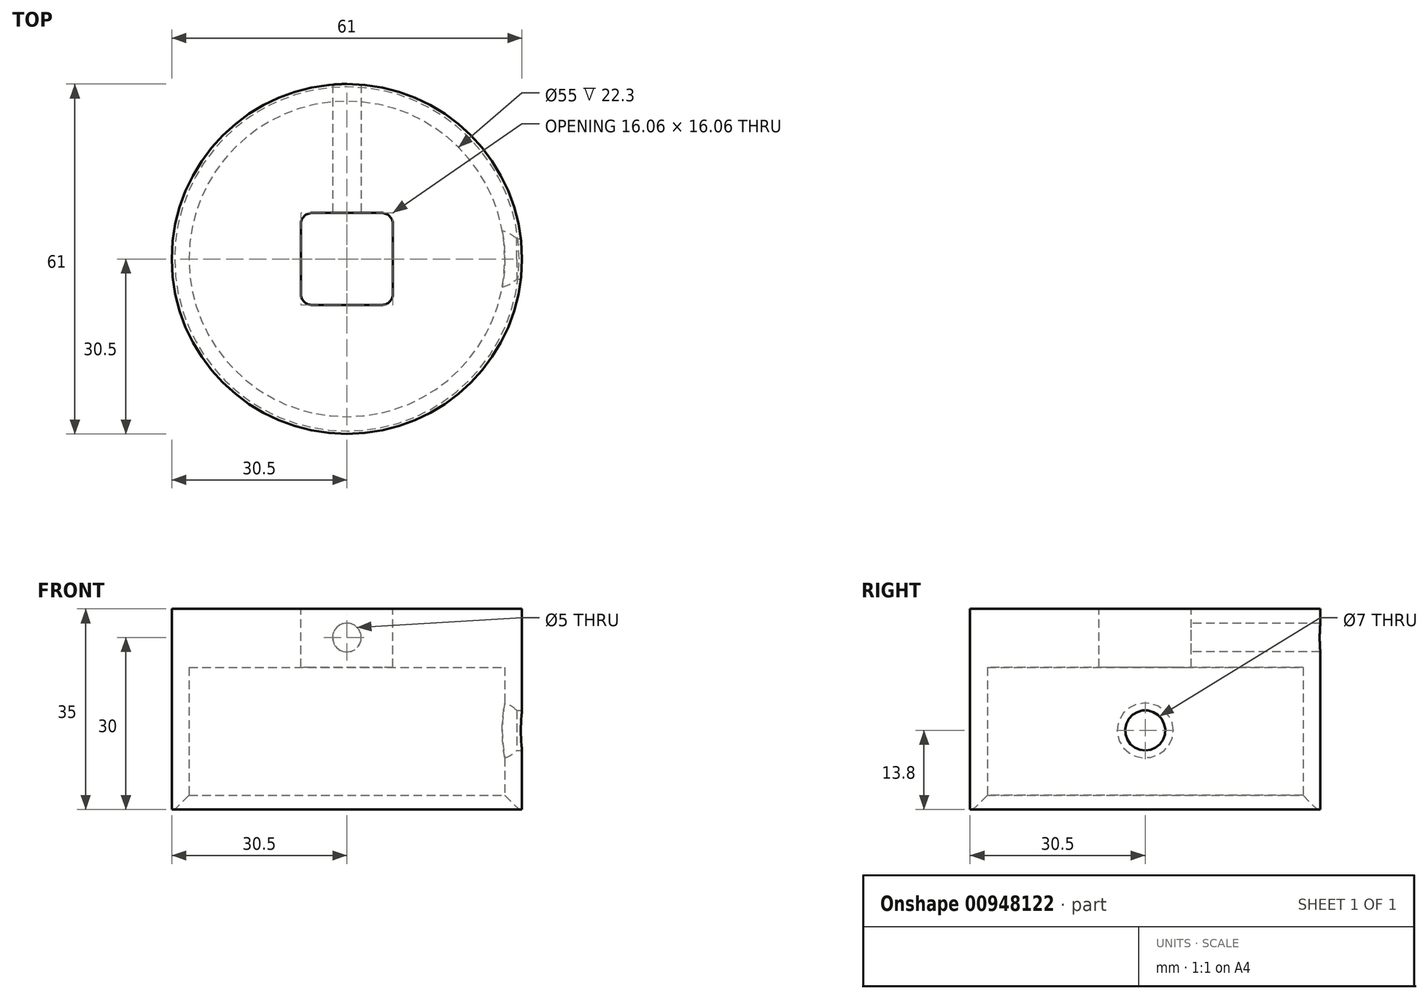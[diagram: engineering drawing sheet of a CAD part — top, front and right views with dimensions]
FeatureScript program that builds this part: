
annotation { "Feature Type Name" : "Feature", "Feature Type Description" : "" }
export const myFeature = defineFeature(function(context is Context, id is Id, definition is map)
    precondition{}
    {
        {
            var Q0;
            Q0=qCreatedBy(makeId("Front.planeOp"),FACE);
            var sketch = newSketch(context, id + "F0", { "sketchPlane" : qUnion([Q0])});
            skLineSegment(sketch, "E0", {"start": v(0, 0) * mm, "end": v(30.5, 0) * mm});
            skLineSegment(sketch, "E1", {"start": v(30.5, 0) * mm, "end": v(30.5, -35) * mm});
            skLineSegment(sketch, "E2", {"start": v(30.5, -35) * mm, "end": v(30, -35) * mm});
            skLineSegment(sketch, "E3", {"start": v(27.5, -32.5) * mm, "end": v(27.5, -10.2) * mm});
            skLineSegment(sketch, "E4", {"start": v(27.5, -10.2) * mm, "end": v(0, -10.2) * mm});
            skLineSegment(sketch, "E5", {"start": v(0, -10.2) * mm, "end": v(0, 0) * mm});
            skLineSegment(sketch, "E6", {"start": v(30, -35) * mm, "end": v(27.5, -32.5) * mm});
            skSolve(sketch);
        }
        {
            var Q0;
            Q0=makeQuery(id+"F0.imprint","IMPRINT",FACE,{"disambiguationData":[TD([[makeQuery(id+"F0.imprint","IMPRINT",EDGE,{"derivedFrom":sQuery(id+"F0.wireOp",EDGE,"E0")}),-1.0]])]});
            var Q1;
            Q1=sQuery(id+"F0.wireOp",EDGE,"E5");
            revolve(context, id + "F1", {"surfaceOperationType" : NewSurfaceOperationType.NEW, "entities" : qUnion([Q0]), "axis" : qUnion([Q1]), "revolveType" : RevolveType.FULL});
        }
        {
            var Q0;
            Q0=makeQuery(id+"F1.opRevolve","SWEPT_FACE",FACE,{"disambiguationData":[OSD([sQuery(id+"F0.wireOp",EDGE,"E0")])]});
            var sketch = newSketch(context, id + "F2", { "sketchPlane" : qUnion([Q0])});
            skLineSegment(sketch, "E7.bottom", {"start": v(6.03, 8.03) * mm, "end": v(-6.03, 8.03) * mm});
            skLineSegment(sketch, "E7.top", {"start": v(6.03, -8.03) * mm, "end": v(-6.03, -8.03) * mm});
            skLineSegment(sketch, "E7.left", {"start": v(8.03, 6.03) * mm, "end": v(8.03, -6.03) * mm});
            skLineSegment(sketch, "E7.right", {"start": v(-8.03, 6.03) * mm, "end": v(-8.03, -6.03) * mm});
            skPoint(sketch, "E7.middle", {"position": v(0, 0) * mm});
            skPoint(sketch, "E8.visualSharp", {"position": v(-8.03, 8.03) * mm});
            skArc(sketch, "E8.filletArc", {"start": v(-6.03, 8.03) * mm, "mid": v(-7.44, 7.44) * mm, "end": v(-8.03, 6.03) * mm});
            skPoint(sketch, "E9.visualSharp", {"position": v(8.03, 8.03) * mm});
            skArc(sketch, "E9.filletArc", {"start": v(8.03, 6.03) * mm, "mid": v(7.44, 7.44) * mm, "end": v(6.03, 8.03) * mm});
            skPoint(sketch, "E10.visualSharp", {"position": v(8.03, -8.03) * mm});
            skArc(sketch, "E10.filletArc", {"start": v(6.03, -8.03) * mm, "mid": v(7.44, -7.44) * mm, "end": v(8.03, -6.03) * mm});
            skPoint(sketch, "E11.visualSharp", {"position": v(-8.03, -8.03) * mm});
            skArc(sketch, "E11.filletArc", {"start": v(-8.03, -6.03) * mm, "mid": v(-7.44, -7.44) * mm, "end": v(-6.03, -8.03) * mm});
            skSolve(sketch);
        }
        {
            var Q0;
            Q0 = qSketchRegion(id + "F2", true);
            extrude(context, id + "F3", {"entities" : qUnion([Q0]), "operationType" : NewBodyOperationType.REMOVE, "oppositeDirection" : true, "depth" : 25 * mm, "offsetDistance" : 25 * mm});
        }
        {
            var Q0;
            Q0=makeQuery(id+"F3.boolean.opBoolean","COPY",FACE,{"derivedFrom":makeQuery(id+"F3.opExtrude","SWEPT_FACE",FACE,{"disambiguationData":[OSD([sQuery(id+"F2.wireOp",EDGE,"E7.bottom")])]})});
            var sketch = newSketch(context, id + "F4", { "sketchPlane" : qUnion([Q0])});
            skCircle(sketch, "E12", {"center": v(0, -5) * mm, "radius": 2.5 * mm});
            skPoint(sketch, "E12.centerSnap0", {"position": v(0, 0) * mm});
            skSolve(sketch);
        }
        {
            var Q0;
            Q0=makeQuery(id+"F4.imprint","IMPRINT",FACE,{"disambiguationData":[TD([[makeQuery(id+"F4.imprint","IMPRINT",EDGE,{"derivedFrom":sQuery(id+"F4.wireOp",EDGE,"E12")}),1.0]])]});
            extrude(context, id + "F5", {"entities" : qUnion([Q0]), "operationType" : NewBodyOperationType.REMOVE, "endBound" : BoundingType.THROUGH_ALL, "oppositeDirection" : true, "depth" : 25 * mm, "offsetDistance" : 25 * mm});
        }
        {
            var Q0;
            Q0=qCreatedBy(makeId("Front.planeOp"),FACE);
            var sketch = newSketch(context, id + "F6", { "sketchPlane" : qUnion([Q0])});
            skArc(sketch, "E13", {"start": v(26, -26.2) * mm, "mid": v(31, -21.2) * mm, "end": v(26, -16.2) * mm});
            skLineSegment(sketch, "E14", {"start": v(26, -16.2) * mm, "end": v(26, -26.2) * mm});
            skSolve(sketch);
        }
        {
            var Q0;
            Q0 = qSketchRegion(id + "F6", true);
            var Q1;
            Q1=sQuery(id+"F6.wireOp",EDGE,"E14");
            revolve(context, id + "F7", {"operationType" : NewBodyOperationType.REMOVE, "surfaceOperationType" : NewSurfaceOperationType.NEW, "entities" : qUnion([Q0]), "axis" : qUnion([Q1]), "revolveType" : RevolveType.FULL, "oppositeDirection" : true});
        }
        {
            var Q0;
            Q0=qCreatedBy(makeId("Right.planeOp"),FACE);
            cPlane(context, id + "F8", {"entities" : qUnion([Q0]), "cplaneType" : CPlaneType.OFFSET, "offset" : 30.5 * mm, "width" : 150 * mm, "height" : 150 * mm});
        }
        {
            var Q0;
            Q0=qCreatedBy(id+"F8.planeOp",FACE);
            var sketch = newSketch(context, id + "F9", { "sketchPlane" : qUnion([Q0])});
            skCircle(sketch, "E15", {"center": v(0, -21.2) * mm, "radius": 3.5 * mm});
            skSolve(sketch);
        }
        {
            var Q0;
            Q0 = qSketchRegion(id + "F9", true);
            extrude(context, id + "F10", {"entities" : qUnion([Q0]), "operationType" : NewBodyOperationType.REMOVE, "oppositeDirection" : true, "depth" : 5 * mm, "offsetDistance" : 25 * mm});
        }
    });
